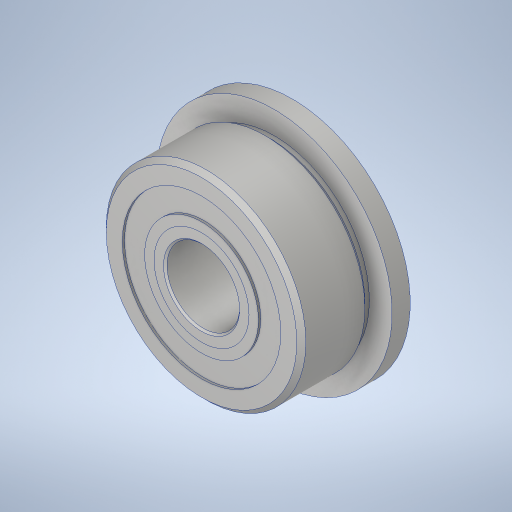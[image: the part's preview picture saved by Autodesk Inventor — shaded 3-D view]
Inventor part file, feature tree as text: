
AUTODESK INVENTOR PART (.ipt)
format: ipt  version: 2023.4 (Build 274418000, 418)  size: 733,696 bytes
history: native  units: in
note: dims shown in document units (in); Inventor stores cm internally (conversion verified against a paired STEP export)
features: other x12, revolve x3
ambient origin geometry x8: Origin, YZ Plane, XZ Plane, XY Plane, X Axis, Y Axis, Z Axis, Center Point
bodies: Solid1 (feature_tree), Solid2 (feature_tree), Solid3 (feature_tree), Solid4 (feature_tree), Solid5 (feature_tree), Solid6 (feature_tree), Solid7 (feature_tree), Solid8 (feature_tree), Solid9 (feature_tree), Solid10 (feature_tree), Solid11 (feature_tree), Solid12 (feature_tree), Solid13 (feature_tree), Solid14 (feature_tree), Solid15 (feature_tree)
feature tree (15):
  revolve  "Revolve2"  [1 undecoded]
  revolve  "Revolve4"  [1 undecoded]
  other  "Cut-Revolve1"
  revolve  "Revolve6[1]"  [1 undecoded]
  other  "CirPattern1[1]"
  other  "CirPattern1[2]"
  other  "CirPattern1[3]"
  other  "CirPattern1[4]"
  other  "CirPattern1[5]"
  other  "CirPattern1[6]"
  other  "CirPattern1[7]"
  other  "CirPattern1[8]"
  other  "CirPattern1[9]"
  other  "Cut-Extrude1"
  other  "Cut-Extrude2"
note: 3 required parameter values undecoded (feature->parameter linkage not recoverable at this tier; creation-order binding heuristic only, values carry confidence <= 0.55)
